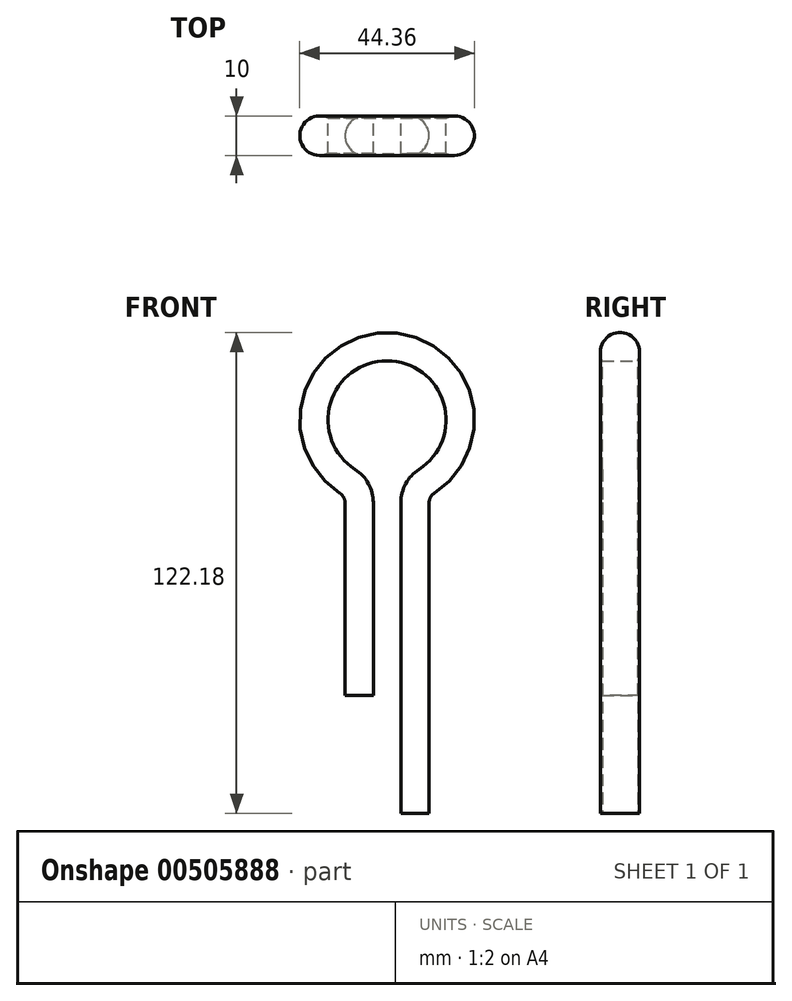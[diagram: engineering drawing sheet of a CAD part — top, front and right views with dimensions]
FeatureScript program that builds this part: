
annotation { "Feature Type Name" : "Feature", "Feature Type Description" : "" }
export const myFeature = defineFeature(function(context is Context, id is Id, definition is map)
    precondition{}
    {
        {
            var Q0;
            Q0=qCreatedBy(makeId("Front.planeOp"),FACE);
            var sketch = newSketch(context, id + "F0", { "sketchPlane" : qUnion([Q0])});
            skArc(sketch, "E0", {"start": v(8.1, -12.62) * mm, "mid": v(0, 15) * mm, "end": v(-8.1, -12.62) * mm});
            skLineSegment(sketch, "E1", {"start": v(3.5, -21.04) * mm, "end": v(3.5, -100) * mm});
            skArc(sketch, "E2", {"start": v(8.1, -12.62) * mm, "mid": v(4.73, -16.25) * mm, "end": v(3.5, -21.04) * mm});
            skLineSegment(sketch, "E3", {"start": v(0, 0) * mm, "end": v(0, -71.25) * mm, "construction": true});
            skLineSegment(sketch, "E4", {"start": v(-3.5, -21.04) * mm, "end": v(-3.5, -70) * mm});
            skArc(sketch, "E5", {"start": v(-3.5, -21.04) * mm, "mid": v(-4.73, -16.25) * mm, "end": v(-8.1, -12.62) * mm});
            skSolve(sketch);
        }
        {
            var Q0;
            Q0=qCreatedBy(makeId("Top.planeOp"),FACE);
            var Q1;
            Q1=sQuery(id+"F0.wireOp",VERTEX,"E4.end");
            cPlane(context, id + "F1", {"entities" : qUnion([Q0, Q1]), "cplaneType" : CPlaneType.PLANE_POINT, "offset" : 25 * mm, "width" : 150 * mm, "height" : 150 * mm});
        }
        {
            var Q0;
            Q0=qCreatedBy(id+"F1.planeOp",FACE);
            var sketch = newSketch(context, id + "F2", { "sketchPlane" : qUnion([Q0])});
            skArc(sketch, "E6", {"start": v(-3.5, 4.5) * mm, "mid": v(-10.68, 0) * mm, "end": v(-3.5, -4.5) * mm});
            skLineSegment(sketch, "E7", {"start": v(-3.5, -4.5) * mm, "end": v(-3.5, 4.5) * mm});
            skPoint(sketch, "E8", {"position": v(-3.5, 0) * mm});
            skSolve(sketch);
        }
        {
            var Q0;
            Q0=makeQuery(id+"F2.imprint","IMPRINT",FACE,{"disambiguationData":[TD([[makeQuery(id+"F2.imprint","IMPRINT",EDGE,{"derivedFrom":sQuery(id+"F2.wireOp",EDGE,"E6")}),1.0]])]});
            var Q1;
            Q1 = qConstructionFilter(qBodyType(qCreatedBy(id + "F0" ,EDGE), BodyType.WIRE), ConstructionObject.NO);
            sweep(context, id + "F3", {"profiles" : qUnion([Q0]), "path" : qUnion([Q1])});
        }
    });
